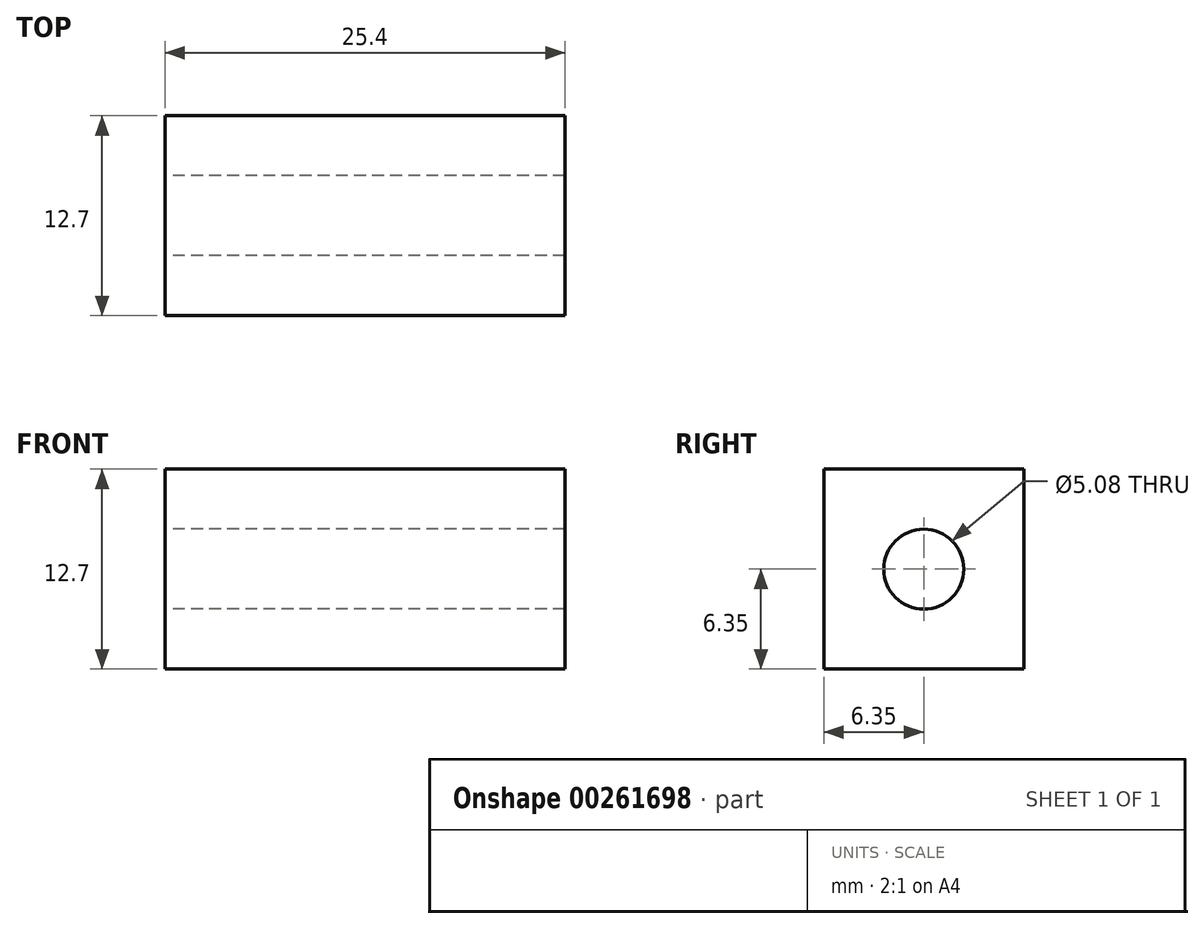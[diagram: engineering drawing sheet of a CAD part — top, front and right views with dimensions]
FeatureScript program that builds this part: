
annotation { "Feature Type Name" : "Feature", "Feature Type Description" : "" }
export const myFeature = defineFeature(function(context is Context, id is Id, definition is map)
    precondition{}
    {
        {
            var Q0;
            Q0=qCreatedBy(makeId("Right.planeOp"),FACE);
            var sketch = newSketch(context, id + "F0", { "sketchPlane" : qUnion([Q0])});
            skLineSegment(sketch, "E0.bottom", {"start": v(0, 0) * mm, "end": v(-12.7, 0) * mm});
            skLineSegment(sketch, "E0.top", {"start": v(0, -12.7) * mm, "end": v(-12.7, -12.7) * mm});
            skLineSegment(sketch, "E0.left", {"start": v(0, 0) * mm, "end": v(0, -12.7) * mm});
            skLineSegment(sketch, "E0.right", {"start": v(-12.7, 0) * mm, "end": v(-12.7, -12.7) * mm});
            skLineSegment(sketch, "E1", {"start": v(-6.35, 0) * mm, "end": v(-6.35, -12.7) * mm});
            skLineSegment(sketch, "E2", {"start": v(0, -6.35) * mm, "end": v(-12.7, -6.35) * mm});
            skCircle(sketch, "E3", {"center": v(-6.35, -6.35) * mm, "radius": 2.54 * mm});
            skSolve(sketch);
        }
        {
            var Q0;
            {var subQ1=sQuery(id+"F0.wireOp",EDGE,"E0.left");var subQ6=sQuery(id+"F0.wireOp",EDGE,"E0.bottom");var subQ9=makeQuery(id+"F0.imprint","INTERSECT",VERTEX,{"derivedFrom":[subQ6,subQ1]});Q0=makeQuery(id+"F0.imprint","IMPRINT",FACE,{"disambiguationData":[TD([[makeQuery(id+"F0.imprint","IMPRINT",EDGE,{"disambiguationData":[TD([[subQ9,-1.0]])],"derivedFrom":subQ6}),1.0]])]});}
            var Q1;
            {var subQ1=sQuery(id+"F0.wireOp",EDGE,"E0.right");var subQ6=sQuery(id+"F0.wireOp",EDGE,"E0.bottom");var subQ9=makeQuery(id+"F0.imprint","INTERSECT",VERTEX,{"derivedFrom":[subQ6,subQ1]});Q1=makeQuery(id+"F0.imprint","IMPRINT",FACE,{"disambiguationData":[TD([[makeQuery(id+"F0.imprint","IMPRINT",EDGE,{"disambiguationData":[TD([[subQ9,1.0]])],"derivedFrom":subQ6}),1.0]])]});}
            var Q2;
            {var subQ1=sQuery(id+"F0.wireOp",EDGE,"E0.right");var subQ6=sQuery(id+"F0.wireOp",EDGE,"E0.top");var subQ9=makeQuery(id+"F0.imprint","INTERSECT",VERTEX,{"derivedFrom":[subQ6,subQ1]});Q2=makeQuery(id+"F0.imprint","IMPRINT",FACE,{"disambiguationData":[TD([[makeQuery(id+"F0.imprint","IMPRINT",EDGE,{"disambiguationData":[TD([[subQ9,1.0]])],"derivedFrom":subQ6}),-1.0]])]});}
            var Q3;
            {var subQ1=sQuery(id+"F0.wireOp",EDGE,"E0.top");var subQ5=sQuery(id+"F0.wireOp",EDGE,"E0.left");var subQ6=makeQuery(id+"F0.imprint","INTERSECT",VERTEX,{"derivedFrom":[subQ1,subQ5]});Q3=makeQuery(id+"F0.imprint","IMPRINT",FACE,{"disambiguationData":[TD([[makeQuery(id+"F0.imprint","IMPRINT",EDGE,{"disambiguationData":[TD([[subQ6,-1.0]])],"derivedFrom":subQ1}),-1.0]])]});}
            extrude(context, id + "F1", {"entities" : qUnion([Q0, Q1, Q2, Q3]), "depth" : 25.4 * mm});
        }
    });
